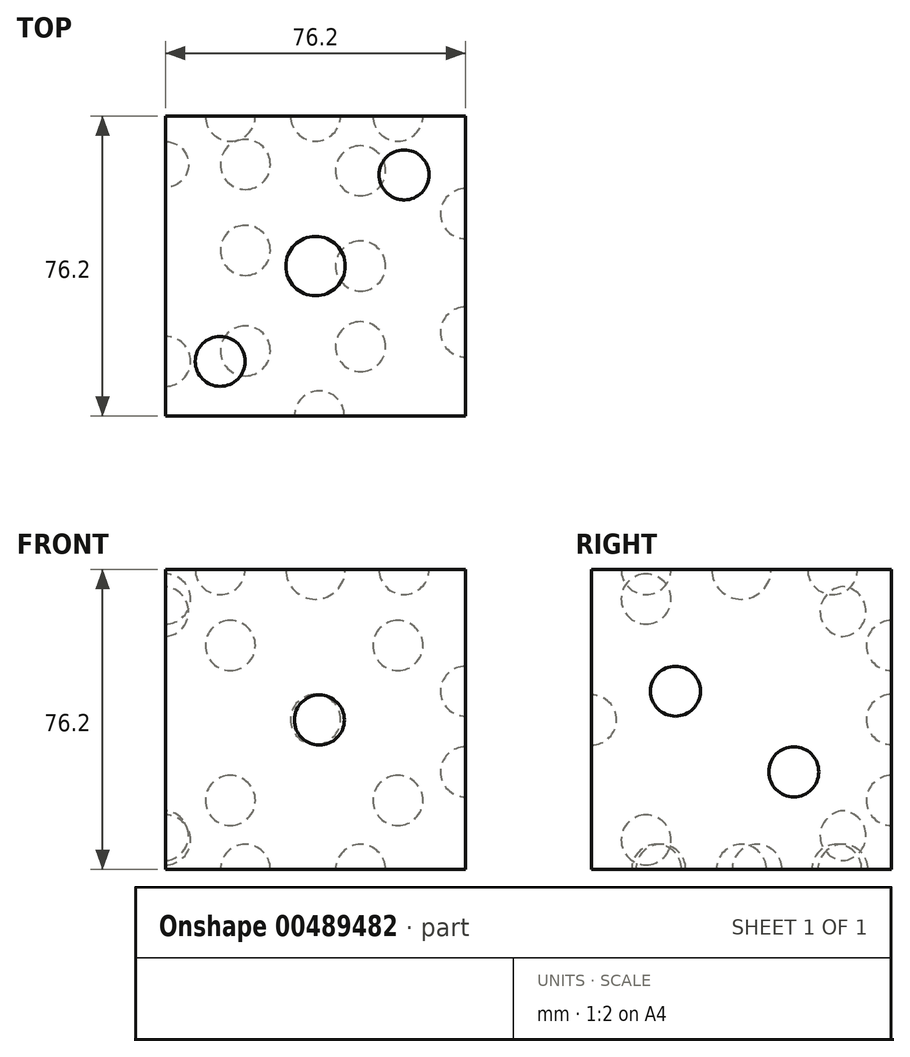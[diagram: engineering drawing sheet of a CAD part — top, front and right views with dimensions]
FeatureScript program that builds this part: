
annotation { "Feature Type Name" : "Feature", "Feature Type Description" : "" }
export const myFeature = defineFeature(function(context is Context, id is Id, definition is map)
    precondition{}
    {
        {
            var Q0;
            Q0=qCreatedBy(makeId("Front.planeOp"),FACE);
            var sketch = newSketch(context, id + "F0", { "sketchPlane" : qUnion([Q0])});
            skLineSegment(sketch, "E0", {"start": v(0, 0) * mm, "end": v(76.2, 0) * mm});
            skLineSegment(sketch, "E1", {"start": v(76.2, 0) * mm, "end": v(76.2, 76.2) * mm});
            skLineSegment(sketch, "E2", {"start": v(76.2, 76.2) * mm, "end": v(0, 76.2) * mm});
            skLineSegment(sketch, "E3", {"start": v(0, 76.2) * mm, "end": v(0, 0) * mm});
            skSolve(sketch);
        }
        {
            var Q0;
            Q0=makeQuery(id+"F0.imprint","IMPRINT",FACE,{"disambiguationData":[TD([[makeQuery(id+"F0.imprint","IMPRINT",EDGE,{"derivedFrom":sQuery(id+"F0.wireOp",EDGE,"E0")}),1.0]])]});
            extrude(context, id + "F1", {"entities" : qUnion([Q0]), "depth" : 76.2 * mm});
        }
        {
            var Q0;
            Q0=qCreatedBy(makeId("Front.planeOp"),FACE);
            cPlane(context, id + "F2", {"entities" : qUnion([Q0]), "cplaneType" : CPlaneType.OFFSET, "offset" : 76.2 * mm, "width" : 152.4 * mm, "height" : 152.4 * mm});
        }
        {
            var Q0;
            Q0=qCreatedBy(id+"F2.planeOp",FACE);
            var sketch = newSketch(context, id + "F3", { "sketchPlane" : qUnion([Q0])});
            skArc(sketch, "E4", {"start": v(39.06, 31.62) * mm, "mid": v(45.4, 37.97) * mm, "end": v(39.06, 44.32) * mm});
            skLineSegment(sketch, "E5", {"start": v(39.06, 76.02) * mm, "end": v(39.06, 0) * mm});
            skSolve(sketch);
        }
        {
            var Q0;
            Q0 = qSketchRegion(id + "F3", true);
            var Q1;
            Q1=sQuery(id+"F3.wireOp",EDGE,"E5");
            revolve(context, id + "F4", {"operationType" : NewBodyOperationType.REMOVE, "entities" : qUnion([Q0]), "axis" : qUnion([Q1]), "revolveType" : RevolveType.FULL, "oppositeDirection" : true});
        }
        {
            var Q0;
            Q0=makeQuery(id+"F1.opExtrude","SWEPT_FACE",FACE,{"disambiguationData":[OSD([sQuery(id+"F0.wireOp",EDGE,"E2")])]});
            var sketch = newSketch(context, id + "F5", { "sketchPlane" : qUnion([Q0])});
            skLineSegment(sketch, "E6", {"start": v(0, 0) * mm, "end": v(76.2, 0) * mm});
            skLineSegment(sketch, "E7", {"start": v(0, -76.2) * mm, "end": v(76.2, -76.2) * mm});
            skArc(sketch, "E8", {"start": v(13.88, -68.67) * mm, "mid": v(20.23, -62.32) * mm, "end": v(13.88, -55.97) * mm});
            skArc(sketch, "E9", {"start": v(33.58, -48.97) * mm, "mid": v(39.93, -42.62) * mm, "end": v(33.58, -36.27) * mm});
            skArc(sketch, "E10", {"start": v(54.86, -27.69) * mm, "mid": v(61.21, -21.34) * mm, "end": v(54.86, -14.99) * mm});
            skLineSegment(sketch, "E11", {"start": v(13.88, 0) * mm, "end": v(13.88, -76.2) * mm});
            skLineSegment(sketch, "E12", {"start": v(33.58, -76.2) * mm, "end": v(33.58, 0) * mm});
            skLineSegment(sketch, "E13", {"start": v(54.86, 0) * mm, "end": v(54.86, -76.2) * mm});
            skSolve(sketch);
        }
        {
            var Q0;
            Q0=makeQuery(id+"F1.opExtrude","SWEPT_FACE",FACE,{"disambiguationData":[OSD([sQuery(id+"F0.wireOp",EDGE,"E1")])]});
            var sketch = newSketch(context, id + "F6", { "sketchPlane" : qUnion([Q0])});
            skArc(sketch, "E14", {"start": v(-52.2, 45.85) * mm, "mid": v(-45.85, 52.2) * mm, "end": v(-52.2, 58.55) * mm});
            skArc(sketch, "E15", {"start": v(-24.8, 18.44) * mm, "mid": v(-18.44, 24.8) * mm, "end": v(-24.8, 31.14) * mm});
            skLineSegment(sketch, "E16", {"start": v(-52.2, 76.2) * mm, "end": v(-52.2, 0) * mm});
            skLineSegment(sketch, "E17", {"start": v(-24.8, 0) * mm, "end": v(-24.8, 76.2) * mm});
            skSolve(sketch);
        }
        {
            var Q0;
            {var subQ0=sQuery(id+"F6.wireOp",EDGE,"E15");Q0=makeQuery(id+"F6.imprint","IMPRINT",FACE,{"disambiguationData":[TD([[makeQuery(id+"F6.imprint","IMPRINT",EDGE,{"derivedFrom":subQ0}),1.0]])]});}
            var Q1;
            Q1=sQuery(id+"F6.wireOp",EDGE,"E17");
            revolve(context, id + "F7", {"operationType" : NewBodyOperationType.REMOVE, "entities" : qUnion([Q0]), "axis" : qUnion([Q1]), "revolveType" : RevolveType.FULL, "oppositeDirection" : true});
        }
        {
            var Q0;
            Q0=makeQuery(id+"F1.opExtrude","SWEPT_FACE",FACE,{"disambiguationData":[OSD([sQuery(id+"F0.wireOp",EDGE,"E1")])]});
            var sketch = newSketch(context, id + "F8", { "sketchPlane" : qUnion([Q0])});
            skLineSegment(sketch, "E18", {"start": v(-54.86, 76.2) * mm, "end": v(-54.86, 0) * mm});
            skArc(sketch, "E19", {"start": v(-54.86, 38.93) * mm, "mid": v(-48.51, 45.28) * mm, "end": v(-54.86, 51.63) * mm});
            skSolve(sketch);
        }
        {
            var Q0;
            {var subQ0=sQuery(id+"F8.wireOp",EDGE,"E19");Q0=makeQuery(id+"F8.imprint","IMPRINT",FACE,{"disambiguationData":[TD([[makeQuery(id+"F8.imprint","IMPRINT",EDGE,{"derivedFrom":subQ0}),1.0]])]});}
            var Q1;
            Q1=sQuery(id+"F8.wireOp",EDGE,"E18");
            revolve(context, id + "F9", {"operationType" : NewBodyOperationType.REMOVE, "entities" : qUnion([Q0]), "axis" : qUnion([Q1]), "revolveType" : RevolveType.FULL, "oppositeDirection" : true});
        }
        {
            var Q0;
            {var subQ0=sQuery(id+"F5.wireOp",EDGE,"E8");Q0=makeQuery(id+"F5.imprint","IMPRINT",FACE,{"disambiguationData":[TD([[makeQuery(id+"F5.imprint","IMPRINT",EDGE,{"derivedFrom":subQ0}),1.0]])]});}
            var Q1;
            Q1=sQuery(id+"F5.wireOp",EDGE,"E11");
            revolve(context, id + "F10", {"operationType" : NewBodyOperationType.REMOVE, "entities" : qUnion([Q0]), "axis" : qUnion([Q1]), "revolveType" : RevolveType.FULL, "oppositeDirection" : true});
        }
        {
            var Q0;
            Q0=makeQuery(id+"F1.opExtrude","SWEPT_FACE",FACE,{"disambiguationData":[OSD([sQuery(id+"F0.wireOp",EDGE,"E2")])]});
            var sketch = newSketch(context, id + "F11", { "sketchPlane" : qUnion([Q0])});
            skLineSegment(sketch, "E20", {"start": v(38.1, 0) * mm, "end": v(38.1, -76.2) * mm});
            skLineSegment(sketch, "E21", {"start": v(60.48, 0) * mm, "end": v(61.06, -76.2) * mm});
            skArc(sketch, "E22", {"start": v(60.64, -21.3) * mm, "mid": v(66.94, -14.9) * mm, "end": v(60.54, -8.6) * mm});
            skPoint(sketch, "E23.center.orphan", {"position": v(38.1, -38.1) * mm});
            skSolve(sketch);
        }
        {
            var Q0;
            {var subQ0=sQuery(id+"F11.wireOp",EDGE,"E23");Q0=makeQuery(id+"F11.imprint","IMPRINT",FACE,{"disambiguationData":[TD([[makeQuery(id+"F11.imprint","IMPRINT",EDGE,{"derivedFrom":subQ0}),1.0]])]});}
            var Q1;
            {var subQ0=sQuery(id+"F11.wireOp",EDGE,"E22");Q1=makeQuery(id+"F11.imprint","IMPRINT",FACE,{"disambiguationData":[TD([[makeQuery(id+"F11.imprint","IMPRINT",EDGE,{"derivedFrom":subQ0}),1.0]])]});}
            var Q2;
            Q2=sQuery(id+"F11.wireOp",EDGE,"E21");
            revolve(context, id + "F12", {"operationType" : NewBodyOperationType.REMOVE, "entities" : qUnion([Q0, Q1]), "axis" : qUnion([Q2]), "revolveType" : RevolveType.FULL, "oppositeDirection" : true});
        }
        {
            var Q0;
            Q0=makeQuery(id+"F1.opExtrude","SWEPT_FACE",FACE,{"disambiguationData":[OSD([sQuery(id+"F0.wireOp",EDGE,"E2")])]});
            var sketch = newSketch(context, id + "F13", { "sketchPlane" : qUnion([Q0])});
            skLineSegment(sketch, "E24", {"start": v(38.1, 0) * mm, "end": v(38.1, -76.2) * mm});
            skArc(sketch, "E25", {"start": v(38.1, -45.65) * mm, "mid": v(45.65, -38.1) * mm, "end": v(38.1, -30.55) * mm});
            skSolve(sketch);
        }
        {
            var Q0;
            {var subQ0=sQuery(id+"F13.wireOp",EDGE,"E25");Q0=makeQuery(id+"F13.imprint","IMPRINT",FACE,{"disambiguationData":[TD([[makeQuery(id+"F13.imprint","IMPRINT",EDGE,{"derivedFrom":subQ0}),1.0]])]});}
            var Q1;
            Q1=sQuery(id+"F13.wireOp",EDGE,"E24");
            revolve(context, id + "F14", {"operationType" : NewBodyOperationType.REMOVE, "entities" : qUnion([Q0]), "axis" : qUnion([Q1]), "revolveType" : RevolveType.FULL, "oppositeDirection" : true});
        }
        {
            var Q0;
            Q0=makeQuery(id+"F1.opExtrude","SWEPT_FACE",FACE,{"disambiguationData":[OSD([sQuery(id+"F0.wireOp",EDGE,"E3")])]});
            var sketch = newSketch(context, id + "F15", { "sketchPlane" : qUnion([Q0])});
            skPoint(sketch, "E26.endSnap0", {"position": v(38.1, 0) * mm});
            skLineSegment(sketch, "E27", {"start": v(62.32, 76.2) * mm, "end": v(62.32, 0) * mm});
            skArc(sketch, "E28", {"start": v(62.32, 62.35) * mm, "mid": v(68.67, 68.7) * mm, "end": v(62.32, 75.05) * mm});
            skArc(sketch, "E29", {"start": v(62.32, 1.15) * mm, "mid": v(68.67, 7.5) * mm, "end": v(62.32, 13.85) * mm});
            skSolve(sketch);
        }
        {
            var Q0;
            {var subQ0=sQuery(id+"F15.wireOp",EDGE,"6cjuZgtX-Fpuy-ClWp-uUv7-zxxIFeHApkAa");Q0=makeQuery(id+"F15.imprint","IMPRINT",FACE,{"disambiguationData":[TD([[makeQuery(id+"F15.imprint","IMPRINT",EDGE,{"derivedFrom":subQ0}),1.0]])]});}
            var Q1;
            {var subQ0=sQuery(id+"F15.wireOp",EDGE,"BcP5bBti-E23h-Rt2S-f24Y-Ruy1ziMdD6hD");Q1=makeQuery(id+"F15.imprint","IMPRINT",FACE,{"disambiguationData":[TD([[makeQuery(id+"F15.imprint","IMPRINT",EDGE,{"derivedFrom":subQ0}),1.0]])]});}
            var Q2;
            {var subQ0=sQuery(id+"F15.wireOp",EDGE,"E29");Q2=makeQuery(id+"F15.imprint","IMPRINT",FACE,{"disambiguationData":[TD([[makeQuery(id+"F15.imprint","IMPRINT",EDGE,{"derivedFrom":subQ0}),1.0]])]});}
            var Q3;
            {var subQ0=sQuery(id+"F15.wireOp",EDGE,"E28");Q3=makeQuery(id+"F15.imprint","IMPRINT",FACE,{"disambiguationData":[TD([[makeQuery(id+"F15.imprint","IMPRINT",EDGE,{"derivedFrom":subQ0}),1.0]])]});}
            var Q4;
            Q4=sQuery(id+"F15.wireOp",EDGE,"E27");
            revolve(context, id + "F16", {"operationType" : NewBodyOperationType.REMOVE, "entities" : qUnion([Q0, Q1, Q2, Q3]), "axis" : qUnion([Q4]), "revolveType" : RevolveType.FULL, "oppositeDirection" : true});
        }
        {
            var Q0;
            Q0=makeQuery(id+"F1.opExtrude","SWEPT_FACE",FACE,{"disambiguationData":[OSD([sQuery(id+"F0.wireOp",EDGE,"E3")])]});
            var sketch = newSketch(context, id + "F17", { "sketchPlane" : qUnion([Q0])});
            skArc(sketch, "E30", {"start": v(12.29, 59.18) * mm, "mid": v(18.1, 65.5) * mm, "end": v(12.29, 71.84) * mm});
            skArc(sketch, "E31", {"start": v(12.29, 2.24) * mm, "mid": v(18.1, 8.56) * mm, "end": v(12.29, 14.9) * mm});
            skLineSegment(sketch, "E32", {"start": v(12.29, 76.2) * mm, "end": v(12.29, 2.24) * mm});
            skSolve(sketch);
        }
        {
            var Q0;
            {var subQ0=sQuery(id+"F17.wireOp",EDGE,"E30");Q0=makeQuery(id+"F17.imprint","IMPRINT",FACE,{"disambiguationData":[TD([[makeQuery(id+"F17.imprint","IMPRINT",EDGE,{"derivedFrom":subQ0}),1.0]])]});}
            var Q1;
            {var subQ0=sQuery(id+"F17.wireOp",EDGE,"E31");Q1=makeQuery(id+"F17.imprint","IMPRINT",FACE,{"disambiguationData":[TD([[makeQuery(id+"F17.imprint","IMPRINT",EDGE,{"derivedFrom":subQ0}),1.0]])]});}
            var Q2;
            Q2=sQuery(id+"F17.wireOp",EDGE,"E32");
            revolve(context, id + "F18", {"operationType" : NewBodyOperationType.REMOVE, "entities" : qUnion([Q0, Q1]), "axis" : qUnion([Q2]), "revolveType" : RevolveType.FULL, "oppositeDirection" : true});
        }
        {
            var Q0;
            Q0=makeQuery(id+"F1.opExtrude","CAP_FACE",FACE,{"disambiguationData":[OSD([sQuery(id+"F0.wireOp",EDGE,"E0"),sQuery(id+"F0.wireOp",EDGE,"E1"),sQuery(id+"F0.wireOp",EDGE,"E2"),sQuery(id+"F0.wireOp",EDGE,"E3")])],"isStart":true});
            var sketch = newSketch(context, id + "F19", { "sketchPlane" : qUnion([Q0])});
            skLineSegment(sketch, "E33", {"start": v(-38.1, 76.2) * mm, "end": v(-38.1, 0) * mm});
            skArc(sketch, "E34", {"start": v(-38.1, 31.75) * mm, "mid": v(-31.75, 38.1) * mm, "end": v(-38.1, 44.45) * mm});
            skSolve(sketch);
        }
        {
            var Q0;
            {var subQ0=sQuery(id+"F19.wireOp",EDGE,"E34");Q0=makeQuery(id+"F19.imprint","IMPRINT",FACE,{"disambiguationData":[TD([[makeQuery(id+"F19.imprint","IMPRINT",EDGE,{"derivedFrom":subQ0}),1.0]])]});}
            var Q1;
            Q1=sQuery(id+"F19.wireOp",EDGE,"E33");
            revolve(context, id + "F20", {"operationType" : NewBodyOperationType.REMOVE, "entities" : qUnion([Q0]), "axis" : qUnion([Q1]), "revolveType" : RevolveType.FULL, "oppositeDirection" : true});
        }
        {
            var Q0;
            Q0=makeQuery(id+"F1.opExtrude","CAP_FACE",FACE,{"disambiguationData":[OSD([sQuery(id+"F0.wireOp",EDGE,"E0"),sQuery(id+"F0.wireOp",EDGE,"E1"),sQuery(id+"F0.wireOp",EDGE,"E2"),sQuery(id+"F0.wireOp",EDGE,"E3")])],"isStart":true});
            var sketch = newSketch(context, id + "F21", { "sketchPlane" : qUnion([Q0])});
            skLineSegment(sketch, "E35", {"start": v(-59.03, 76.2) * mm, "end": v(-59.03, 0) * mm});
            skArc(sketch, "E36", {"start": v(-59.03, 50.55) * mm, "mid": v(-52.68, 56.9) * mm, "end": v(-59.03, 63.25) * mm});
            skArc(sketch, "E37", {"start": v(-59.03, 11.17) * mm, "mid": v(-52.68, 17.52) * mm, "end": v(-59.03, 23.87) * mm});
            skSolve(sketch);
        }
        {
            var Q0;
            {var subQ0=sQuery(id+"F21.wireOp",EDGE,"E36");Q0=makeQuery(id+"F21.imprint","IMPRINT",FACE,{"disambiguationData":[TD([[makeQuery(id+"F21.imprint","IMPRINT",EDGE,{"derivedFrom":subQ0}),1.0]])]});}
            var Q1;
            {var subQ0=sQuery(id+"F21.wireOp",EDGE,"E37");Q1=makeQuery(id+"F21.imprint","IMPRINT",FACE,{"disambiguationData":[TD([[makeQuery(id+"F21.imprint","IMPRINT",EDGE,{"derivedFrom":subQ0}),1.0]])]});}
            var Q2;
            Q2=sQuery(id+"F21.wireOp",EDGE,"E35");
            revolve(context, id + "F22", {"operationType" : NewBodyOperationType.REMOVE, "entities" : qUnion([Q0, Q1]), "axis" : qUnion([Q2]), "revolveType" : RevolveType.FULL, "oppositeDirection" : true});
        }
        {
            var Q0;
            Q0=makeQuery(id+"F1.opExtrude","CAP_FACE",FACE,{"disambiguationData":[OSD([sQuery(id+"F0.wireOp",EDGE,"E0"),sQuery(id+"F0.wireOp",EDGE,"E1"),sQuery(id+"F0.wireOp",EDGE,"E2"),sQuery(id+"F0.wireOp",EDGE,"E3")])],"isStart":true});
            var sketch = newSketch(context, id + "F23", { "sketchPlane" : qUnion([Q0])});
            skLineSegment(sketch, "E38", {"start": v(-16.45, 76.2) * mm, "end": v(-16.45, 0) * mm});
            skArc(sketch, "E39", {"start": v(-16.45, 50.55) * mm, "mid": v(-10.1, 56.9) * mm, "end": v(-16.45, 63.25) * mm});
            skArc(sketch, "E40", {"start": v(-16.45, 11.17) * mm, "mid": v(-10.1, 17.52) * mm, "end": v(-16.45, 23.87) * mm});
            skSolve(sketch);
        }
        {
            var Q0;
            {var subQ0=sQuery(id+"F23.wireOp",EDGE,"E39");Q0=makeQuery(id+"F23.imprint","IMPRINT",FACE,{"disambiguationData":[TD([[makeQuery(id+"F23.imprint","IMPRINT",EDGE,{"derivedFrom":subQ0}),1.0]])]});}
            var Q1;
            {var subQ0=sQuery(id+"F23.wireOp",EDGE,"E40");Q1=makeQuery(id+"F23.imprint","IMPRINT",FACE,{"disambiguationData":[TD([[makeQuery(id+"F23.imprint","IMPRINT",EDGE,{"derivedFrom":subQ0}),1.0]])]});}
            var Q2;
            Q2=sQuery(id+"F23.wireOp",EDGE,"E38");
            revolve(context, id + "F24", {"operationType" : NewBodyOperationType.REMOVE, "entities" : qUnion([Q0, Q1]), "axis" : qUnion([Q2]), "revolveType" : RevolveType.FULL, "oppositeDirection" : true});
        }
        {
            var Q0;
            Q0=makeQuery(id+"F1.opExtrude","SWEPT_FACE",FACE,{"disambiguationData":[OSD([sQuery(id+"F0.wireOp",EDGE,"E0")])]});
            var sketch = newSketch(context, id + "F25", { "sketchPlane" : qUnion([Q0])});
            skLineSegment(sketch, "E41", {"start": v(20.27, 76.2) * mm, "end": v(20.27, 0) * mm});
            skLineSegment(sketch, "E42", {"start": v(48.48, 76.2) * mm, "end": v(48.48, 0) * mm});
            skArc(sketch, "E43", {"start": v(20.27, 53.3) * mm, "mid": v(26.62, 59.65) * mm, "end": v(20.27, 66) * mm});
            skArc(sketch, "E44", {"start": v(20.27, 27.76) * mm, "mid": v(26.62, 34.1) * mm, "end": v(20.27, 40.46) * mm});
            skArc(sketch, "E45", {"start": v(20.27, 5.94) * mm, "mid": v(26.62, 12.29) * mm, "end": v(20.27, 18.64) * mm});
            skArc(sketch, "E46", {"start": v(48.48, 54.37) * mm, "mid": v(54.83, 60.72) * mm, "end": v(48.48, 67.07) * mm});
            skArc(sketch, "E47", {"start": v(48.48, 27.76) * mm, "mid": v(54.83, 34.1) * mm, "end": v(48.48, 40.46) * mm});
            skPoint(sketch, "E47.centerSnap0", {"position": v(48.48, 38.1) * mm});
            skArc(sketch, "E48", {"start": v(48.48, 5.4) * mm, "mid": v(54.83, 11.76) * mm, "end": v(48.48, 18.1) * mm});
            skSolve(sketch);
        }
        {
            var Q0;
            {var subQ0=sQuery(id+"F25.wireOp",EDGE,"E43");Q0=makeQuery(id+"F25.imprint","IMPRINT",FACE,{"disambiguationData":[TD([[makeQuery(id+"F25.imprint","IMPRINT",EDGE,{"derivedFrom":subQ0}),1.0]])]});}
            var Q1;
            {var subQ0=sQuery(id+"F25.wireOp",EDGE,"E44");Q1=makeQuery(id+"F25.imprint","IMPRINT",FACE,{"disambiguationData":[TD([[makeQuery(id+"F25.imprint","IMPRINT",EDGE,{"derivedFrom":subQ0}),1.0]])]});}
            var Q2;
            {var subQ0=sQuery(id+"F25.wireOp",EDGE,"E45");Q2=makeQuery(id+"F25.imprint","IMPRINT",FACE,{"disambiguationData":[TD([[makeQuery(id+"F25.imprint","IMPRINT",EDGE,{"derivedFrom":subQ0}),1.0]])]});}
            var Q3;
            Q3=sQuery(id+"F25.wireOp",EDGE,"E41");
            revolve(context, id + "F26", {"operationType" : NewBodyOperationType.REMOVE, "entities" : qUnion([Q0, Q1, Q2]), "axis" : qUnion([Q3]), "revolveType" : RevolveType.FULL, "oppositeDirection" : true});
        }
        {
            var Q0;
            Q0=makeQuery(id+"F1.opExtrude","SWEPT_FACE",FACE,{"disambiguationData":[OSD([sQuery(id+"F0.wireOp",EDGE,"E0")])]});
            var sketch = newSketch(context, id + "F27", { "sketchPlane" : qUnion([Q0])});
            skLineSegment(sketch, "E49", {"start": v(49.54, 76.2) * mm, "end": v(49.54, 0) * mm});
            skArc(sketch, "E50", {"start": v(49.54, 52.24) * mm, "mid": v(55.9, 58.59) * mm, "end": v(49.54, 64.94) * mm});
            skArc(sketch, "E51", {"start": v(49.54, 31.75) * mm, "mid": v(55.9, 38.1) * mm, "end": v(49.54, 44.45) * mm});
            skArc(sketch, "E52", {"start": v(49.54, 7.53) * mm, "mid": v(55.9, 13.88) * mm, "end": v(49.54, 20.23) * mm});
            skSolve(sketch);
        }
        {
            var Q0;
            {var subQ0=sQuery(id+"F27.wireOp",EDGE,"E50");Q0=makeQuery(id+"F27.imprint","IMPRINT",FACE,{"disambiguationData":[TD([[makeQuery(id+"F27.imprint","IMPRINT",EDGE,{"derivedFrom":subQ0}),1.0]])]});}
            var Q1;
            {var subQ0=sQuery(id+"F27.wireOp",EDGE,"E51");Q1=makeQuery(id+"F27.imprint","IMPRINT",FACE,{"disambiguationData":[TD([[makeQuery(id+"F27.imprint","IMPRINT",EDGE,{"derivedFrom":subQ0}),1.0]])]});}
            var Q2;
            {var subQ0=sQuery(id+"F27.wireOp",EDGE,"E52");Q2=makeQuery(id+"F27.imprint","IMPRINT",FACE,{"disambiguationData":[TD([[makeQuery(id+"F27.imprint","IMPRINT",EDGE,{"derivedFrom":subQ0}),1.0]])]});}
            var Q3;
            Q3=sQuery(id+"F27.wireOp",EDGE,"E49");
            revolve(context, id + "F28", {"operationType" : NewBodyOperationType.REMOVE, "entities" : qUnion([Q0, Q1, Q2]), "axis" : qUnion([Q3]), "revolveType" : RevolveType.FULL, "oppositeDirection" : true});
        }
    });
